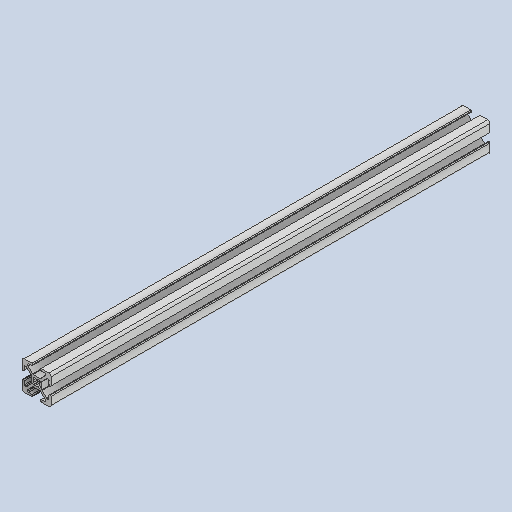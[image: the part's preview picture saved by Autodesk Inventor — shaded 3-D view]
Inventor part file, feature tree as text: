
AUTODESK INVENTOR PART (.ipt)
format: ipt  version: 2022 (Build 260153000, 153)  size: 286,720 bytes
history: native  units: in
note: dims shown in document units (in); Inventor stores cm internally (conversion verified against a paired STEP export)
features: other x3, sketch x1
ambient origin geometry x8: Origin, YZ Plane, XZ Plane, XY Plane, X Axis, Y Axis, Z Axis, Center Point
bodies: Solid1 (feature_tree)
feature tree (4):
  other  "20x20x301.4 T Slot Extrusion Bar.ipt"
  other  "Solid1::20x20x301.4 T Slot Extrusion Bar.ipt"
  other  "TaggingFeature1"
  sketch  "Sketch_1"  dims[d0=0.3937in]
